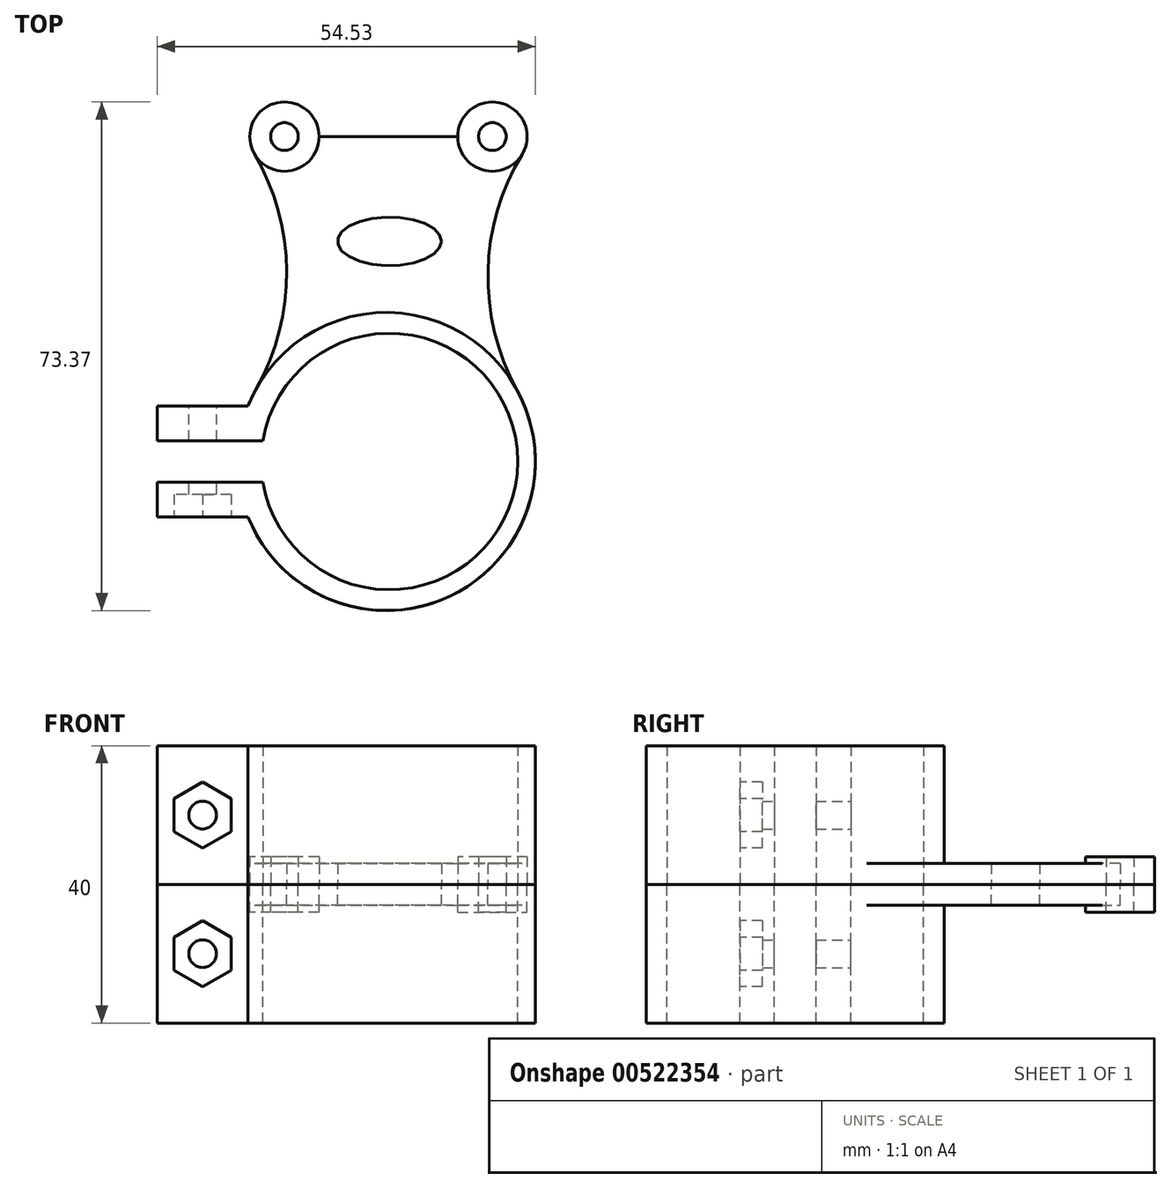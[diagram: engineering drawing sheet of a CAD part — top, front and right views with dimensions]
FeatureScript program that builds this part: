
annotation { "Feature Type Name" : "Feature", "Feature Type Description" : "" }
export const myFeature = defineFeature(function(context is Context, id is Id, definition is map)
    precondition{}
    {
        {
            var Q0;
            Q0=qCreatedBy(makeId("Top.planeOp"),FACE);
            var sketch = newSketch(context, id + "F0", { "sketchPlane" : qUnion([Q0])});
            skArc(sketch, "E0", {"start": v(-18.26, -2.84) * mm, "mid": v(18.5, 0.16) * mm, "end": v(-18.26, 3.16) * mm});
            skLineSegment(sketch, "E1", {"start": v(0, 0) * mm, "end": v(0, -51.02) * mm, "construction": true});
            skLineSegment(sketch, "E2", {"start": v(-15.16, 47.03) * mm, "end": v(14.84, 47.03) * mm});
            skCircle(sketch, "E3", {"center": v(-15.16, 47.03) * mm, "radius": 2 * mm});
            skCircle(sketch, "E4", {"center": v(14.84, 47.03) * mm, "radius": 2 * mm});
            skCircle(sketch, "E5.0", {"center": v(14.84, 47.03) * mm, "radius": 5 * mm});
            skCircle(sketch, "E6.0", {"center": v(-15.16, 47.03) * mm, "radius": 5 * mm});
            skPoint(sketch, "E7.orphan", {"position": v(0, 15) * mm});
            skPoint(sketch, "E8.end.orphan", {"position": v(0, -15) * mm});
            skPoint(sketch, "E9.orphan", {"position": v(0, 21.5) * mm});
            skPoint(sketch, "E10.orphan", {"position": v(0, -21.34) * mm});
            skPoint(sketch, "E11.orphan", {"position": v(-20.16, 47.03) * mm});
            skPoint(sketch, "E12.orphan", {"position": v(19.84, 47.03) * mm});
            skEllipse(sketch, "E13", {"center": v(0, 31.94) * mm, "majorRadius": 7.5 * mm, "minorRadius": 3.5 * mm, "majorAxis": v(1, 0)});
            skLineSegment(sketch, "E14.bottom", {"start": v(-33.5, -5.84) * mm, "end": v(-33.5, -2.84) * mm});
            skPoint(sketch, "E14.middle", {"position": v(-21.5, 0) * mm});
            skLineSegment(sketch, "E15.0", {"start": v(-33.5, 3.16) * mm, "end": v(-21.29, 3.16) * mm});
            skLineSegment(sketch, "E16.0", {"start": v(-33.5, -2.84) * mm, "end": v(-21.29, -2.84) * mm});
            skPoint(sketch, "E17.trimOffspring.end.orphan", {"position": v(-9.5, -6.16) * mm});
            skPoint(sketch, "E18.trimOffspring.end.orphan", {"position": v(-9.5, 5.84) * mm});
            skLineSegment(sketch, "E19.trimOffspring", {"start": v(-33.5, 3.16) * mm, "end": v(-33.5, 6.16) * mm});
            skArc(sketch, "E20.trimOffspring", {"start": v(-20.42, -7.84) * mm, "mid": v(21.03, 0.16) * mm, "end": v(-20.42, 8.16) * mm});
            skLineSegment(sketch, "E21", {"start": v(-21.29, 3.16) * mm, "end": v(-18.26, 3.16) * mm});
            skLineSegment(sketch, "E22", {"start": v(-21.29, -2.84) * mm, "end": v(-18.26, -2.84) * mm});
            skLineSegment(sketch, "E23", {"start": v(-33.5, -5.84) * mm, "end": v(-33.5, -7.84) * mm});
            skLineSegment(sketch, "E24", {"start": v(-33.5, -7.84) * mm, "end": v(-20.42, -7.84) * mm});
            skLineSegment(sketch, "E25", {"start": v(-33.5, 6.16) * mm, "end": v(-33.5, 8.16) * mm});
            skLineSegment(sketch, "E26", {"start": v(-33.5, 8.16) * mm, "end": v(-20.42, 8.16) * mm});
            skPoint(sketch, "E27.endSnap0", {"position": v(-5.46, 31.94) * mm});
            skArc(sketch, "E28", {"start": v(-19.2, 10.7) * mm, "mid": v(-14.84, 27.64) * mm, "end": v(-19.48, 44.51) * mm});
            skArc(sketch, "E29", {"start": v(19.12, 44.44) * mm, "mid": v(14.21, 27.57) * mm, "end": v(18.39, 10.5) * mm});
            skSolve(sketch);
        }
        {
            var Q0;
            Q0=makeQuery(id+"F0.imprint","IMPRINT",FACE,{"disambiguationData":[TD([[makeQuery(id+"F0.imprint","IMPRINT",EDGE,{"derivedFrom":sQuery(id+"F0.wireOp",EDGE,"E0")}),-1.0]])]});
            extrude(context, id + "F1", {"entities" : qUnion([Q0]), "depth" : 20 * mm, "offsetDistance" : 25 * mm});
        }
        {
            var Q0;
            {var subQ1=sQuery(id+"F0.wireOp",EDGE,"a4KQXwT9-HFvs-ruFt-iuDf-gMoE4k8AScbi");Q0=makeQuery(id+"F0.imprint","IMPRINT",FACE,{"disambiguationData":[TD([[makeQuery(id+"F0.imprint","IMPRINT",EDGE,{"derivedFrom":subQ1}),-1.0]])]});}
            var Q1;
            Q1=makeQuery(id+"F0.imprint","IMPRINT",FACE,{"disambiguationData":[TD([[makeQuery(id+"F0.imprint","IMPRINT",EDGE,{"derivedFrom":sQuery(id+"F0.wireOp",EDGE,"E13")}),-1.0]])]});
            var Q2;
            Q2=makeQuery(id+"F0.imprint","IMPRINT",FACE,{"disambiguationData":[TD([[makeQuery(id+"F0.imprint","IMPRINT",EDGE,{"derivedFrom":sQuery(id+"F0.wireOp",EDGE,"E3")}),-1.0]])]});
            var Q3;
            Q3=makeQuery(id+"F0.imprint","IMPRINT",FACE,{"disambiguationData":[TD([[makeQuery(id+"F0.imprint","IMPRINT",EDGE,{"derivedFrom":sQuery(id+"F0.wireOp",EDGE,"E4")}),-1.0]])]});
            extrude(context, id + "F2", {"entities" : qUnion([Q0, Q1, Q2, Q3]), "operationType" : NewBodyOperationType.ADD, "depth" : 3 * mm, "offsetDistance" : 25 * mm});
        }
        {
            var Q0;
            Q0=makeQuery(id+"F0.imprint","IMPRINT",FACE,{"disambiguationData":[TD([[makeQuery(id+"F0.imprint","IMPRINT",EDGE,{"derivedFrom":sQuery(id+"F0.wireOp",EDGE,"E3")}),-1.0]])]});
            var Q1;
            Q1=makeQuery(id+"F0.imprint","IMPRINT",FACE,{"disambiguationData":[TD([[makeQuery(id+"F0.imprint","IMPRINT",EDGE,{"derivedFrom":sQuery(id+"F0.wireOp",EDGE,"E4")}),-1.0]])]});
            extrude(context, id + "F3", {"entities" : qUnion([Q0, Q1]), "operationType" : NewBodyOperationType.ADD, "depth" : 4 * mm, "offsetDistance" : 25 * mm});
        }
        {
            var Q0;
            Q0=makeQuery(id+"F1.opExtrude","SWEPT_FACE",FACE,{"disambiguationData":[OSD([sQuery(id+"F0.wireOp",EDGE,"E24")])]});
            var sketch = newSketch(context, id + "F4", { "sketchPlane" : qUnion([Q0])});
            skCircle(sketch, "E30.cCircle", {"center": v(-26.96, 10) * mm, "radius": 4.12 * mm, "construction": true});
            skPoint(sketch, "E30.cCircle.centerSnap0", {"position": v(-33.5, 10) * mm});
            skPoint(sketch, "E30.cCircle.centerSnap1", {"position": v(-26.96, 0) * mm});
            skLineSegment(sketch, "E30.0", {"start": v(-31.09, 7.62) * mm, "end": v(-31.09, 12.38) * mm});
            skLineSegment(sketch, "E30.1", {"start": v(-31.09, 12.38) * mm, "end": v(-26.96, 14.76) * mm});
            skLineSegment(sketch, "E30.2", {"start": v(-26.96, 14.76) * mm, "end": v(-22.84, 12.38) * mm});
            skLineSegment(sketch, "E30.3", {"start": v(-22.84, 12.38) * mm, "end": v(-22.84, 7.62) * mm});
            skLineSegment(sketch, "E30.4", {"start": v(-22.84, 7.62) * mm, "end": v(-26.96, 5.24) * mm});
            skLineSegment(sketch, "E30.5", {"start": v(-26.96, 5.24) * mm, "end": v(-31.09, 7.62) * mm});
            skPoint(sketch, "E30.0.midPoint", {"position": v(-31.09, 10) * mm});
            skSolve(sketch);
        }
        {
            var Q0;
            Q0=makeQuery(id+"F4.imprint","IMPRINT",FACE,{"disambiguationData":[TD([[makeQuery(id+"F4.imprint","IMPRINT",EDGE,{"derivedFrom":sQuery(id+"F4.wireOp",EDGE,"E30.0")}),-1.0]])]});
            extrude(context, id + "F5", {"entities" : qUnion([Q0]), "operationType" : NewBodyOperationType.REMOVE, "oppositeDirection" : true, "depth" : 3.25 * mm, "offsetDistance" : 25 * mm});
        }
        {
            var Q0;
            Q0=makeQuery(id+"F1.opExtrude","SWEPT_FACE",FACE,{"disambiguationData":[OSD([sQuery(id+"F0.wireOp",EDGE,"E26")])]});
            var sketch = newSketch(context, id + "F6", { "sketchPlane" : qUnion([Q0])});
            skCircle(sketch, "E31", {"center": v(26.96, 10) * mm, "radius": 2 * mm});
            skPoint(sketch, "E31.centerSnap0", {"position": v(33.5, 10) * mm});
            skPoint(sketch, "E31.centerSnap1", {"position": v(26.96, 0) * mm});
            skSolve(sketch);
        }
        {
            var Q0;
            Q0=makeQuery(id+"F6.imprint","IMPRINT",FACE,{"disambiguationData":[TD([[makeQuery(id+"F6.imprint","IMPRINT",EDGE,{"derivedFrom":sQuery(id+"F6.wireOp",EDGE,"E31")}),1.0]])]});
            extrude(context, id + "F7", {"entities" : qUnion([Q0]), "operationType" : NewBodyOperationType.REMOVE, "endBound" : BoundingType.THROUGH_ALL, "oppositeDirection" : true, "depth" : 25 * mm, "offsetDistance" : 25 * mm});
        }
        {
            var Q0;
            Q0=makeQuery(id+"F1.opExtrude","SWEPT_BODY",BODY,{"disambiguationData":[OSD([sQuery(id+"F0.wireOp",EDGE,"E0"),sQuery(id+"F0.wireOp",EDGE,"E14.bottom"),sQuery(id+"F0.wireOp",EDGE,"E15.0"),sQuery(id+"F0.wireOp",EDGE,"E16.0"),sQuery(id+"F0.wireOp",EDGE,"E19.trimOffspring"),sQuery(id+"F0.wireOp",EDGE,"E20.trimOffspring"),sQuery(id+"F0.wireOp",EDGE,"E21"),sQuery(id+"F0.wireOp",EDGE,"E22"),sQuery(id+"F0.wireOp",EDGE,"E23"),sQuery(id+"F0.wireOp",EDGE,"E24"),sQuery(id+"F0.wireOp",EDGE,"E25"),sQuery(id+"F0.wireOp",EDGE,"E26")])]});
            var Q1;
            Q1=makeQuery(id+"F0.imprint","IMPRINT",FACE,{"disambiguationData":[TD([[makeQuery(id+"F0.imprint","IMPRINT",EDGE,{"derivedFrom":sQuery(id+"F0.wireOp",EDGE,"E13")}),-1.0]])]});
            mirror(context, id + "F8", {"entities" : qUnion([Q0]), "mirrorPlane" : qUnion([Q1])});
        }
    });
